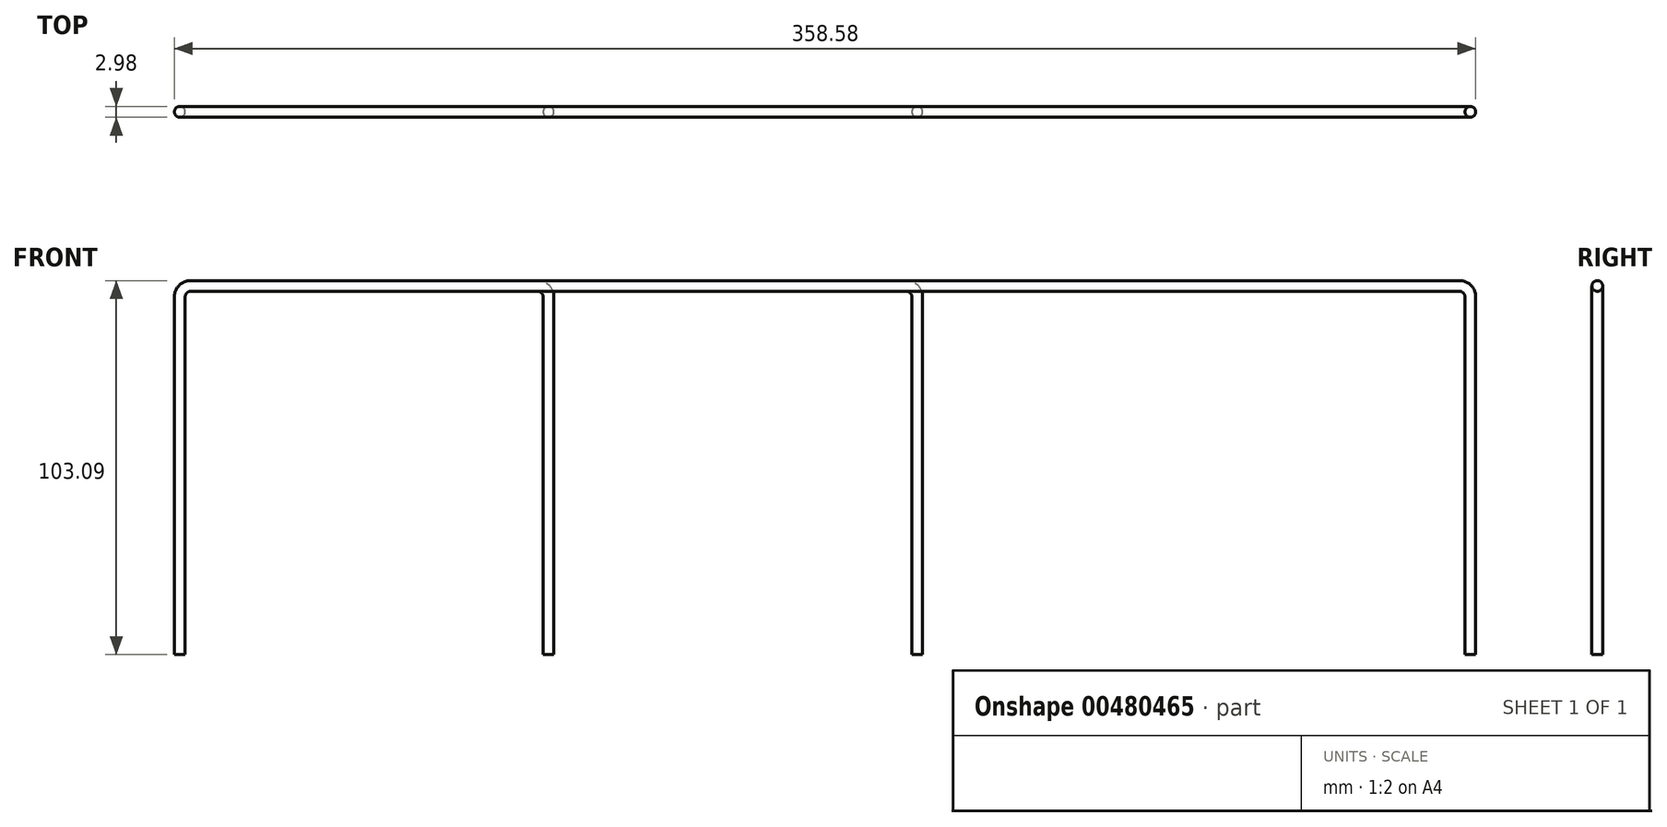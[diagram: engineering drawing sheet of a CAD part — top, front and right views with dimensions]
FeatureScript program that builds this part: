
annotation { "Feature Type Name" : "Feature", "Feature Type Description" : "" }
export const myFeature = defineFeature(function(context is Context, id is Id, definition is map)
    precondition{}
    {
        {
            var Q0;
            Q0=qCreatedBy(makeId("Top.planeOp"),FACE);
            var sketch = newSketch(context, id + "F0", { "sketchPlane" : qUnion([Q0])});
            skCircle(sketch, "E0", {"center": v(0, 0) * mm, "radius": 1.49 * mm});
            skSolve(sketch);
        }
        {
            var Q0;
            Q0=qCreatedBy(makeId("Front.planeOp"),FACE);
            var sketch = newSketch(context, id + "F1", { "sketchPlane" : qUnion([Q0])});
            skLineSegment(sketch, "E1", {"start": v(0, 0) * mm, "end": v(0, 98.63) * mm});
            skLineSegment(sketch, "E2", {"start": v(2.97, 101.6) * mm, "end": v(98.63, 101.6) * mm});
            skLineSegment(sketch, "E3", {"start": v(101.6, 98.63) * mm, "end": v(101.6, 0) * mm});
            skPoint(sketch, "E4.visualSharp", {"position": v(0, 101.6) * mm});
            skArc(sketch, "E4.filletArc", {"start": v(2.97, 101.6) * mm, "mid": v(0.87, 100.73) * mm, "end": v(0, 98.63) * mm});
            skPoint(sketch, "E5.visualSharp", {"position": v(101.6, 101.6) * mm});
            skArc(sketch, "E5.filletArc", {"start": v(101.6, 98.63) * mm, "mid": v(100.73, 100.73) * mm, "end": v(98.63, 101.6) * mm});
            skSolve(sketch);
        }
        {
            var Q0;
            Q0=qCreatedBy(makeId("Front.planeOp"),FACE);
            var sketch = newSketch(context, id + "F2", { "sketchPlane" : qUnion([Q0])});
            skLineSegment(sketch, "E6", {"start": v(0, 0) * mm, "end": v(0, 98.63) * mm});
            skLineSegment(sketch, "E7", {"start": v(2.97, 101.6) * mm, "end": v(200.23, 101.6) * mm});
            skLineSegment(sketch, "E8", {"start": v(203.2, 98.63) * mm, "end": v(203.2, 0) * mm});
            skPoint(sketch, "E9.visualSharp", {"position": v(0, 101.6) * mm});
            skArc(sketch, "E9.filletArc", {"start": v(2.97, 101.6) * mm, "mid": v(0.87, 100.73) * mm, "end": v(0, 98.63) * mm});
            skPoint(sketch, "E10.visualSharp", {"position": v(203.2, 101.6) * mm});
            skArc(sketch, "E10.filletArc", {"start": v(203.2, 98.63) * mm, "mid": v(202.33, 100.73) * mm, "end": v(200.23, 101.6) * mm});
            skSolve(sketch);
        }
        {
            var Q0;
            Q0=qCreatedBy(makeId("Front.planeOp"),FACE);
            var sketch = newSketch(context, id + "F3", { "sketchPlane" : qUnion([Q0])});
            skLineSegment(sketch, "E11", {"start": v(0, 0) * mm, "end": v(0, 98.63) * mm});
            skLineSegment(sketch, "E12", {"start": v(2.97, 101.6) * mm, "end": v(352.63, 101.6) * mm});
            skLineSegment(sketch, "E13", {"start": v(355.6, 98.63) * mm, "end": v(355.6, 0) * mm});
            skPoint(sketch, "E14.visualSharp", {"position": v(0, 101.6) * mm});
            skArc(sketch, "E14.filletArc", {"start": v(2.97, 101.6) * mm, "mid": v(0.87, 100.73) * mm, "end": v(0, 98.63) * mm});
            skPoint(sketch, "E15.visualSharp", {"position": v(355.6, 101.6) * mm});
            skArc(sketch, "E15.filletArc", {"start": v(355.6, 98.63) * mm, "mid": v(354.73, 100.73) * mm, "end": v(352.63, 101.6) * mm});
            skSolve(sketch);
        }
        {
            var Q0;
            Q0 = qSketchRegion(id + "F0", true);
            var Q1;
            Q1 = qConstructionFilter(qBodyType(qCreatedBy(id + "F1" ,EDGE), BodyType.WIRE), ConstructionObject.NO);
            sweep(context, id + "F4", {"profiles" : qUnion([Q0]), "path" : qUnion([Q1])});
        }
        {
            var Q0;
            Q0 = qSketchRegion(id + "F0", true);
            var Q1;
            Q1 = qConstructionFilter(qBodyType(qCreatedBy(id + "F2" ,EDGE), BodyType.WIRE), ConstructionObject.NO);
            sweep(context, id + "F5", {"profiles" : qUnion([Q0]), "path" : qUnion([Q1])});
        }
        {
            var Q0;
            Q0 = qSketchRegion(id + "F0", true);
            var Q1;
            Q1 = qConstructionFilter(qBodyType(qCreatedBy(id + "F3" ,EDGE), BodyType.WIRE), ConstructionObject.NO);
            sweep(context, id + "F6", {"profiles" : qUnion([Q0]), "path" : qUnion([Q1])});
        }
    });
